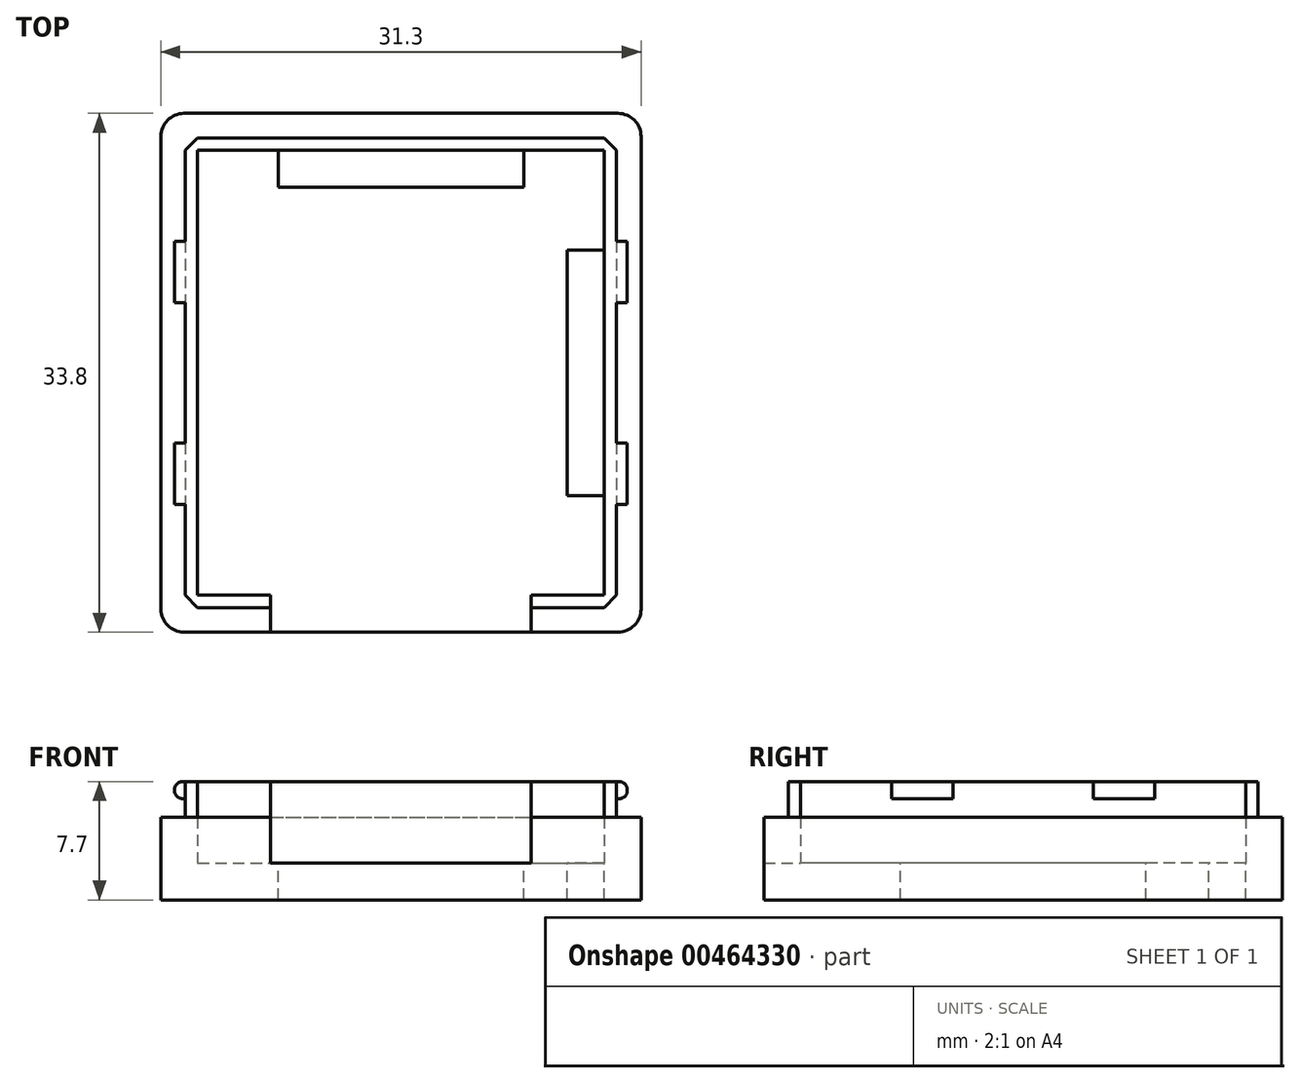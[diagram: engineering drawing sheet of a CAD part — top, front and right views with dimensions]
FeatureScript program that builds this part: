
annotation { "Feature Type Name" : "Feature", "Feature Type Description" : "" }
export const myFeature = defineFeature(function(context is Context, id is Id, definition is map)
    precondition{}
    {
        {
            var Q0;
            Q0=qCreatedBy(makeId("Top.planeOp"),FACE);
            var sketch = newSketch(context, id + "F0", { "sketchPlane" : qUnion([Q0])});
            skLineSegment(sketch, "E0.bottom", {"start": v(-13.25, 14.5) * mm, "end": v(13.25, 14.5) * mm});
            skLineSegment(sketch, "E0.top", {"start": v(-13.25, -14.5) * mm, "end": v(13.25, -14.5) * mm});
            skLineSegment(sketch, "E0.left", {"start": v(-13.25, 14.5) * mm, "end": v(-13.25, -14.5) * mm});
            skLineSegment(sketch, "E0.right", {"start": v(13.25, 14.5) * mm, "end": v(13.25, -14.5) * mm});
            skPoint(sketch, "E0.middle", {"position": v(0, 0) * mm});
            skLineSegment(sketch, "E1.bottom", {"start": v(-15.65, 16.9) * mm, "end": v(15.65, 16.9) * mm});
            skLineSegment(sketch, "E1.top", {"start": v(-15.65, -16.9) * mm, "end": v(15.65, -16.9) * mm});
            skLineSegment(sketch, "E1.left", {"start": v(-15.65, 16.9) * mm, "end": v(-15.65, -16.9) * mm});
            skLineSegment(sketch, "E1.right", {"start": v(15.65, 16.9) * mm, "end": v(15.65, -16.9) * mm});
            skLineSegment(sketch, "E2.bottom", {"start": v(-8, 14.5) * mm, "end": v(8, 14.5) * mm});
            skLineSegment(sketch, "E2.top", {"start": v(-8, 12.1) * mm, "end": v(8, 12.1) * mm});
            skLineSegment(sketch, "E2.left", {"start": v(-8, 14.5) * mm, "end": v(-8, 12.1) * mm});
            skLineSegment(sketch, "E2.right", {"start": v(8, 14.5) * mm, "end": v(8, 12.1) * mm});
            skLineSegment(sketch, "E3.bottom", {"start": v(-13.25, 8) * mm, "end": v(-10.85, 8) * mm});
            skLineSegment(sketch, "E3.top", {"start": v(-13.25, -8) * mm, "end": v(-10.85, -8) * mm});
            skLineSegment(sketch, "E3.left", {"start": v(-13.25, 8) * mm, "end": v(-13.25, -8) * mm});
            skLineSegment(sketch, "E3.right", {"start": v(-10.85, 8) * mm, "end": v(-10.85, -8) * mm});
            skLineSegment(sketch, "E4.MirrorCS", {"start": v(8, -14.5) * mm, "end": v(8, -12.1) * mm});
            skLineSegment(sketch, "E5.MirrorCS", {"start": v(-8, -14.5) * mm, "end": v(-8, -12.1) * mm});
            skLineSegment(sketch, "E6.MirrorCS", {"start": v(-8, -14.5) * mm, "end": v(8, -14.5) * mm});
            skLineSegment(sketch, "E7.MirrorCS", {"start": v(-8, -12.1) * mm, "end": v(8, -12.1) * mm});
            skLineSegment(sketch, "E8.MirrorCS", {"start": v(13.25, 8) * mm, "end": v(13.25, -8) * mm});
            skLineSegment(sketch, "E9.MirrorCS", {"start": v(13.25, -8) * mm, "end": v(10.85, -8) * mm});
            skLineSegment(sketch, "E10.MirrorCS", {"start": v(13.25, 8) * mm, "end": v(10.85, 8) * mm});
            skLineSegment(sketch, "E11.MirrorCS", {"start": v(10.85, 8) * mm, "end": v(10.85, -8) * mm});
            skSolve(sketch);
        }
        {
            var Q0;
            Q0=makeQuery(id+"F0.imprint","IMPRINT",FACE,{"disambiguationData":[TD([[makeQuery(id+"F0.imprint","IMPRINT",EDGE,{"derivedFrom":sQuery(id+"F0.wireOp",EDGE,"E0.bottom")}),-1.0]])]});
            var Q1;
            Q1=makeQuery(id+"F0.imprint","IMPRINT",FACE,{"disambiguationData":[TD([[makeQuery(id+"F0.imprint","IMPRINT",EDGE,{"derivedFrom":sQuery(id+"F0.wireOp",EDGE,"E4.MirrorCS")}),1.0]])]});
            var Q2;
            Q2=makeQuery(id+"F0.imprint","IMPRINT",FACE,{"disambiguationData":[TD([[makeQuery(id+"F0.imprint","IMPRINT",EDGE,{"derivedFrom":sQuery(id+"F0.wireOp",EDGE,"E3.bottom")}),-1.0]])]});
            var Q3;
            Q3=makeQuery(id+"F0.imprint","IMPRINT",FACE,{"disambiguationData":[TD([[makeQuery(id+"F0.imprint","IMPRINT",EDGE,{"derivedFrom":sQuery(id+"F0.wireOp",EDGE,"E8.MirrorCS")}),-1.0]])]});
            var Q4;
            Q4=makeQuery(id+"F0.imprint","IMPRINT",FACE,{"disambiguationData":[TD([[makeQuery(id+"F0.imprint","IMPRINT",EDGE,{"derivedFrom":sQuery(id+"F0.wireOp",EDGE,"E2.bottom")}),-1.0]])]});
            extrude(context, id + "F1", {"entities" : qUnion([Q0, Q1, Q2, Q3, Q4]), "oppositeDirection" : true, "depth" : 3.4 * mm, "hasSecondDirection" : true, "secondDirectionOppositeDirection" : true, "secondDirectionDepth" : 1 * mm, "offsetDistance" : 25 * mm});
        }
        {
            var Q0;
            Q0=makeQuery(id+"F0.imprint","IMPRINT",FACE,{"disambiguationData":[TD([[makeQuery(id+"F0.imprint","IMPRINT",EDGE,{"derivedFrom":sQuery(id+"F0.wireOp",EDGE,"E0.bottom")}),1.0]])]});
            extrude(context, id + "F2", {"entities" : qUnion([Q0]), "operationType" : NewBodyOperationType.ADD, "depth" : 2 * mm, "hasSecondDirection" : true, "secondDirectionOppositeDirection" : true, "secondDirectionDepth" : 3.4 * mm, "offsetDistance" : 25 * mm});
        }
        {
            var Q0;
            Q0=qCreatedBy(makeId("Top.planeOp"),FACE);
            var sketch = newSketch(context, id + "F3", { "sketchPlane" : qUnion([Q0])});
            skLineSegment(sketch, "E12.bottom", {"start": v(-13.25, 8.57) * mm, "end": v(-14.25, 8.57) * mm});
            skLineSegment(sketch, "E12.top", {"start": v(-13.25, 4.57) * mm, "end": v(-14.25, 4.57) * mm});
            skLineSegment(sketch, "E12.left", {"start": v(-13.25, 8.57) * mm, "end": v(-13.25, 4.57) * mm});
            skLineSegment(sketch, "E13.MirrorCS", {"start": v(13.25, 8.57) * mm, "end": v(14.25, 8.57) * mm});
            skLineSegment(sketch, "E14.MirrorCS", {"start": v(13.25, 4.57) * mm, "end": v(14.25, 4.57) * mm});
            skLineSegment(sketch, "E15.MirrorCS", {"start": v(14.25, 8.57) * mm, "end": v(14.25, 4.57) * mm});
            skLineSegment(sketch, "E16.MirrorCS", {"start": v(13.25, 8.57) * mm, "end": v(13.25, 4.57) * mm});
            skLineSegment(sketch, "E17.MirrorCS", {"start": v(14.05, 8.57) * mm, "end": v(14.05, 4.57) * mm});
            skLineSegment(sketch, "E18.bottom", {"start": v(-14.25, 8.57) * mm, "end": v(-14.75, 8.57) * mm});
            skLineSegment(sketch, "E18.top", {"start": v(-14.25, 4.57) * mm, "end": v(-14.75, 4.57) * mm});
            skLineSegment(sketch, "E18.right", {"start": v(-14.75, 8.57) * mm, "end": v(-14.75, 4.57) * mm});
            skLineSegment(sketch, "E19.MirrorCS", {"start": v(14.25, 4.57) * mm, "end": v(14.75, 4.57) * mm});
            skLineSegment(sketch, "E20.MirrorCS", {"start": v(14.75, 8.57) * mm, "end": v(14.75, 4.57) * mm});
            skLineSegment(sketch, "E21.MirrorCS", {"start": v(14.25, 8.57) * mm, "end": v(14.75, 8.57) * mm});
            skLineSegment(sketch, "E22", {"start": v(-14.25, 8.57) * mm, "end": v(-14.25, 4.57) * mm});
            skLineSegment(sketch, "E23", {"start": v(-14.05, 8.57) * mm, "end": v(-14.05, 4.57) * mm});
            skLineSegment(sketch, "E24.MirrorCS", {"start": v(-14.25, -8.57) * mm, "end": v(-14.75, -8.57) * mm});
            skLineSegment(sketch, "E25.MirrorCS", {"start": v(-13.25, -8.57) * mm, "end": v(-14.25, -8.57) * mm});
            skLineSegment(sketch, "E26.MirrorCS", {"start": v(-14.75, -8.57) * mm, "end": v(-14.75, -4.57) * mm});
            skLineSegment(sketch, "E27.MirrorCS", {"start": v(-14.25, -4.57) * mm, "end": v(-14.75, -4.57) * mm});
            skLineSegment(sketch, "E28.MirrorCS", {"start": v(-14.05, -8.57) * mm, "end": v(-14.05, -4.57) * mm});
            skLineSegment(sketch, "E29.MirrorCS", {"start": v(-13.25, -8.57) * mm, "end": v(-13.25, -4.57) * mm});
            skLineSegment(sketch, "E30.MirrorCS", {"start": v(-14.25, -8.57) * mm, "end": v(-14.25, -4.57) * mm});
            skLineSegment(sketch, "E31.MirrorCS", {"start": v(-13.25, -4.57) * mm, "end": v(-14.25, -4.57) * mm});
            skLineSegment(sketch, "E32.MirrorCS", {"start": v(14.25, -4.57) * mm, "end": v(14.75, -4.57) * mm});
            skLineSegment(sketch, "E33.MirrorCS", {"start": v(14.25, -8.57) * mm, "end": v(14.75, -8.57) * mm});
            skLineSegment(sketch, "E34.MirrorCS", {"start": v(14.75, -8.57) * mm, "end": v(14.75, -4.57) * mm});
            skLineSegment(sketch, "E35.MirrorCS", {"start": v(14.05, -8.57) * mm, "end": v(14.05, -4.57) * mm});
            skLineSegment(sketch, "E36.MirrorCS", {"start": v(13.25, -8.57) * mm, "end": v(13.25, -4.57) * mm});
            skLineSegment(sketch, "E37.MirrorCS", {"start": v(13.25, -4.57) * mm, "end": v(14.25, -4.57) * mm});
            skLineSegment(sketch, "E38.MirrorCS", {"start": v(14.25, -8.57) * mm, "end": v(14.25, -4.57) * mm});
            skLineSegment(sketch, "E39.MirrorCS", {"start": v(13.25, -8.57) * mm, "end": v(14.25, -8.57) * mm});
            skSolve(sketch);
        }
        {
            var Q0;
            Q0=makeQuery(id+"F2.opExtrude","CAP_FACE",FACE,{"disambiguationData":[OSD([sQuery(id+"F0.wireOp",EDGE,"E0.bottom"),sQuery(id+"F0.wireOp",EDGE,"E0.top"),sQuery(id+"F0.wireOp",EDGE,"E0.left"),sQuery(id+"F0.wireOp",EDGE,"E0.right"),sQuery(id+"F0.wireOp",EDGE,"E1.bottom"),sQuery(id+"F0.wireOp",EDGE,"E1.top"),sQuery(id+"F0.wireOp",EDGE,"E1.left"),sQuery(id+"F0.wireOp",EDGE,"E1.right"),sQuery(id+"F0.wireOp",EDGE,"E2.bottom"),sQuery(id+"F0.wireOp",EDGE,"E3.left"),sQuery(id+"F0.wireOp",EDGE,"E6.MirrorCS"),sQuery(id+"F0.wireOp",EDGE,"E8.MirrorCS")])],"isStart":false});
            var sketch = newSketch(context, id + "F4", { "sketchPlane" : qUnion([Q0])});
            skLineSegment(sketch, "E40.bottom", {"start": v(-13.25, 14.5) * mm, "end": v(13.25, 14.5) * mm});
            skLineSegment(sketch, "E40.top", {"start": v(-13.25, -14.5) * mm, "end": v(13.25, -14.5) * mm});
            skLineSegment(sketch, "E40.left", {"start": v(-13.25, 14.5) * mm, "end": v(-13.25, -14.5) * mm});
            skLineSegment(sketch, "E40.right", {"start": v(13.25, 14.5) * mm, "end": v(13.25, -14.5) * mm});
            skLineSegment(sketch, "E41.bottom", {"start": v(-14.05, 15.3) * mm, "end": v(14.05, 15.3) * mm});
            skLineSegment(sketch, "E41.top", {"start": v(-14.05, -15.3) * mm, "end": v(14.05, -15.3) * mm});
            skLineSegment(sketch, "E41.left", {"start": v(-14.05, 15.3) * mm, "end": v(-14.05, -15.3) * mm});
            skLineSegment(sketch, "E41.right", {"start": v(14.05, 15.3) * mm, "end": v(14.05, -15.3) * mm});
            skSolve(sketch);
        }
        {
            var Q0;
            Q0 = qSketchRegion(id + "F4", true);
            extrude(context, id + "F5", {"entities" : qUnion([Q0]), "operationType" : NewBodyOperationType.ADD, "depth" : 2.3 * mm, "offsetDistance" : 25 * mm});
        }
        {
            var Q0;
            Q0=qSketchRegion(id+"F3",true);
            extrude(context, id + "F6", {"entities" : qUnion([Q0]), "operationType" : NewBodyOperationType.ADD, "depth" : 2 * mm, "hasSecondDirection" : true, "secondDirectionOppositeDirection" : false, "secondDirectionDepth" : 1.2 * mm});
        }
        {
            var Q0;
            {var subQ2=sQuery(id+"F3.wireOp",EDGE,"E28.MirrorCS");Q0=makeQuery(id+"F3.imprint","IMPRINT",FACE,{"disambiguationData":[TD([[makeQuery(id+"F3.imprint","IMPRINT",EDGE,{"derivedFrom":subQ2}),-1.0]])]});}
            var Q1;
            {var subQ0=sQuery(id+"F3.wireOp",EDGE,"E12.left");Q1=makeQuery(id+"F3.imprint","IMPRINT",FACE,{"disambiguationData":[TD([[makeQuery(id+"F3.imprint","IMPRINT",EDGE,{"derivedFrom":subQ0}),-1.0]])]});}
            var Q2;
            {var subQ0=sQuery(id+"F3.wireOp",EDGE,"E35.MirrorCS");Q2=makeQuery(id+"F3.imprint","IMPRINT",FACE,{"disambiguationData":[TD([[makeQuery(id+"F3.imprint","IMPRINT",EDGE,{"derivedFrom":subQ0}),1.0]])]});}
            var Q3;
            {var subQ0=sQuery(id+"F3.wireOp",EDGE,"E16.MirrorCS");Q3=makeQuery(id+"F3.imprint","IMPRINT",FACE,{"disambiguationData":[TD([[makeQuery(id+"F3.imprint","IMPRINT",EDGE,{"derivedFrom":subQ0}),1.0]])]});}
            extrude(context, id + "F7", {"entities" : qUnion([Q0, Q1, Q2, Q3]), "operationType" : NewBodyOperationType.ADD, "depth" : 4.3 * mm, "hasSecondDirection" : true, "secondDirectionOppositeDirection" : false, "secondDirectionDepth" : 2 * mm});
        }
        {
            var Q0;
            Q0=makeQuery(id+"F3.imprint","IMPRINT",FACE,{"disambiguationData":[TD([[makeQuery(id+"F3.imprint","IMPRINT",EDGE,{"derivedFrom":sQuery(id+"F3.wireOp",EDGE,"E18.bottom")}),1.0]])]});
            var Q1;
            {var subQ0=sQuery(id+"F3.wireOp",EDGE,"E22");Q1=makeQuery(id+"F3.imprint","IMPRINT",FACE,{"disambiguationData":[TD([[makeQuery(id+"F3.imprint","IMPRINT",EDGE,{"derivedFrom":subQ0}),1.0]])]});}
            var Q2;
            Q2=makeQuery(id+"F3.imprint","IMPRINT",FACE,{"disambiguationData":[TD([[makeQuery(id+"F3.imprint","IMPRINT",EDGE,{"derivedFrom":sQuery(id+"F3.wireOp",EDGE,"E24.MirrorCS")}),-1.0]])]});
            var Q3;
            {var subQ2=sQuery(id+"F3.wireOp",EDGE,"E28.MirrorCS");Q3=makeQuery(id+"F3.imprint","IMPRINT",FACE,{"disambiguationData":[TD([[makeQuery(id+"F3.imprint","IMPRINT",EDGE,{"derivedFrom":subQ2}),1.0]])]});}
            var Q4;
            Q4=makeQuery(id+"F3.imprint","IMPRINT",FACE,{"disambiguationData":[TD([[makeQuery(id+"F3.imprint","IMPRINT",EDGE,{"derivedFrom":sQuery(id+"F3.wireOp",EDGE,"E15.MirrorCS")}),1.0]])]});
            var Q5;
            {var subQ0=sQuery(id+"F3.wireOp",EDGE,"E15.MirrorCS");Q5=makeQuery(id+"F3.imprint","IMPRINT",FACE,{"disambiguationData":[TD([[makeQuery(id+"F3.imprint","IMPRINT",EDGE,{"derivedFrom":subQ0}),-1.0]])]});}
            var Q6;
            Q6=makeQuery(id+"F3.imprint","IMPRINT",FACE,{"disambiguationData":[TD([[makeQuery(id+"F3.imprint","IMPRINT",EDGE,{"derivedFrom":sQuery(id+"F3.wireOp",EDGE,"E32.MirrorCS")}),-1.0]])]});
            var Q7;
            {var subQ0=sQuery(id+"F3.wireOp",EDGE,"E35.MirrorCS");Q7=makeQuery(id+"F3.imprint","IMPRINT",FACE,{"disambiguationData":[TD([[makeQuery(id+"F3.imprint","IMPRINT",EDGE,{"derivedFrom":subQ0}),-1.0]])]});}
            extrude(context, id + "F8", {"entities" : qUnion([Q0, Q1, Q2, Q3, Q4, Q5, Q6, Q7]), "operationType" : NewBodyOperationType.ADD, "depth" : 4.3 * mm, "hasSecondDirection" : true, "secondDirectionOppositeDirection" : false, "secondDirectionDepth" : 3.2 * mm});
        }
        {
            var Q0;
            Q0=makeQuery(id+"F6.opExtrude","CAP_EDGE",EDGE,{"disambiguationData":[OSD([sQuery(id+"F3.wireOp",EDGE,"VDrkBrkV-ZUyN-kKdc-6HjS-wqe3Krwlsqec.left")])],"isStart":true});
            var Q1;
            Q1=makeQuery(id+"F6.opExtrude","CAP_EDGE",EDGE,{"disambiguationData":[OSD([sQuery(id+"F3.wireOp",EDGE,"E12.left")])],"isStart":true});
            var Q2;
            Q2=makeQuery(id+"F6.opExtrude","CAP_EDGE",EDGE,{"disambiguationData":[OSD([sQuery(id+"F3.wireOp",EDGE,"9b8740c0-6d80-43f4-a298-cfb8220f7c486.MirrorCS")])],"isStart":true});
            var Q3;
            Q3=makeQuery(id+"F6.opExtrude","CAP_EDGE",EDGE,{"disambiguationData":[OSD([sQuery(id+"F3.wireOp",EDGE,"E16.MirrorCS")])],"isStart":true});
            var Q4;
            Q4=makeQuery(id+"F8.opExtrude","CAP_EDGE",EDGE,{"disambiguationData":[OSD([sQuery(id+"F3.wireOp",EDGE,"13b3b95b-50e3-4c5a-a444-739a302621f31.MirrorCS")])],"isStart":true});
            var Q5;
            Q5=makeQuery(id+"F8.opExtrude","CAP_EDGE",EDGE,{"disambiguationData":[OSD([sQuery(id+"F3.wireOp",EDGE,"13b3b95b-50e3-4c5a-a444-739a302621f31.MirrorCS")])],"isStart":false});
            var Q6;
            Q6=makeQuery(id+"F8.opExtrude","CAP_EDGE",EDGE,{"disambiguationData":[OSD([sQuery(id+"F3.wireOp",EDGE,"E20.MirrorCS")])],"isStart":true});
            var Q7;
            Q7=makeQuery(id+"F8.opExtrude","CAP_EDGE",EDGE,{"disambiguationData":[OSD([sQuery(id+"F3.wireOp",EDGE,"6daNayIJ-oZqj-4Qv5-FHtt-P2iYpOLPTab5.right")])],"isStart":true});
            var Q8;
            Q8=makeQuery(id+"F8.opExtrude","CAP_EDGE",EDGE,{"disambiguationData":[OSD([sQuery(id+"F3.wireOp",EDGE,"E18.right")])],"isStart":true});
            var Q9;
            Q9=makeQuery(id+"F8.opExtrude","CAP_EDGE",EDGE,{"disambiguationData":[OSD([sQuery(id+"F3.wireOp",EDGE,"E18.right")])],"isStart":false});
            var Q10;
            Q10=makeQuery(id+"F8.opExtrude","CAP_EDGE",EDGE,{"disambiguationData":[OSD([sQuery(id+"F3.wireOp",EDGE,"6daNayIJ-oZqj-4Qv5-FHtt-P2iYpOLPTab5.right")])],"isStart":false});
            var Q11;
            Q11=makeQuery(id+"F8.opExtrude","CAP_EDGE",EDGE,{"disambiguationData":[OSD([sQuery(id+"F3.wireOp",EDGE,"E34.MirrorCS")])],"isStart":false});
            var Q12;
            Q12=makeQuery(id+"F8.opExtrude","CAP_EDGE",EDGE,{"disambiguationData":[OSD([sQuery(id+"F3.wireOp",EDGE,"E34.MirrorCS")])],"isStart":true});
            var Q13;
            Q13=makeQuery(id+"F6.opExtrude","CAP_EDGE",EDGE,{"disambiguationData":[OSD([sQuery(id+"F3.wireOp",EDGE,"E36.MirrorCS")])],"isStart":true});
            var Q14;
            Q14=makeQuery(id+"F8.opExtrude","CAP_EDGE",EDGE,{"disambiguationData":[OSD([sQuery(id+"F3.wireOp",EDGE,"E26.MirrorCS")])],"isStart":false});
            var Q15;
            Q15=makeQuery(id+"F8.opExtrude","CAP_EDGE",EDGE,{"disambiguationData":[OSD([sQuery(id+"F3.wireOp",EDGE,"E26.MirrorCS")])],"isStart":true});
            var Q16;
            Q16=makeQuery(id+"F6.opExtrude","CAP_EDGE",EDGE,{"disambiguationData":[OSD([sQuery(id+"F3.wireOp",EDGE,"E29.MirrorCS")])],"isStart":true});
            var Q17;
            Q17=makeQuery(id+"F8.opExtrude","CAP_EDGE",EDGE,{"disambiguationData":[OSD([sQuery(id+"F3.wireOp",EDGE,"E20.MirrorCS")])],"isStart":false});
            fillet(context, id + "F9", {"entities" : qUnion([Q0, Q1, Q2, Q3, Q4, Q5, Q6, Q7, Q8, Q9, Q10, Q11, Q12, Q13, Q14, Q15, Q16, Q17]), "radius" : .5 * mm, "tangentPropagation" : true, "allowEdgeOverflow" : false});
        }
        {
            var Q0;
            Q0=qCreatedBy(makeId("Front.planeOp"),FACE);
            var sketch = newSketch(context, id + "F10", { "sketchPlane" : qUnion([Q0])});
            skLineSegment(sketch, "E42.bottom", {"start": v(-8.5, 6) * mm, "end": v(8.5, 6) * mm});
            skLineSegment(sketch, "E42.top", {"start": v(-8.5, -1) * mm, "end": v(8.5, -1) * mm});
            skLineSegment(sketch, "E42.left", {"start": v(-8.5, 6) * mm, "end": v(-8.5, -1) * mm});
            skLineSegment(sketch, "E42.right", {"start": v(8.5, 6) * mm, "end": v(8.5, -1) * mm});
            skPoint(sketch, "E43", {"position": v(0, 7) * mm});
            skSolve(sketch);
        }
        {
            var Q0;
            Q0=qSketchRegion(id+"F10",true);
            extrude(context, id + "F11", {"entities" : qUnion([Q0]), "operationType" : NewBodyOperationType.REMOVE, "depth" : 18 * mm, "hasSecondDirection" : true, "secondDirectionOppositeDirection" : false, "secondDirectionDepth" : 14 * mm, "offsetDistance" : 25 * mm});
        }
        {
            var Q0;
            Q0=makeQuery(id+"F2.opExtrude","SWEPT_EDGE",EDGE,{"disambiguationData":[OSD([sQuery(id+"F0.wireOp",EDGE,"E1.top"),sQuery(id+"F0.wireOp",EDGE,"E1.right")])]});
            var Q1;
            Q1=makeQuery(id+"F2.opExtrude","SWEPT_EDGE",EDGE,{"disambiguationData":[OSD([sQuery(id+"F0.wireOp",EDGE,"E1.bottom"),sQuery(id+"F0.wireOp",EDGE,"E1.right")])]});
            var Q2;
            Q2=makeQuery(id+"F2.opExtrude","SWEPT_EDGE",EDGE,{"disambiguationData":[OSD([sQuery(id+"F0.wireOp",EDGE,"E1.bottom"),sQuery(id+"F0.wireOp",EDGE,"E1.left")])]});
            var Q3;
            Q3=makeQuery(id+"F2.opExtrude","SWEPT_EDGE",EDGE,{"disambiguationData":[OSD([sQuery(id+"F0.wireOp",EDGE,"E1.top"),sQuery(id+"F0.wireOp",EDGE,"E1.left")])]});
            fillet(context, id + "F12", {"entities" : qUnion([Q0, Q1, Q2, Q3]), "radius" : 1.5 * mm, "tangentPropagation" : true, "allowEdgeOverflow" : false});
        }
        {
            var Q0;
            Q0=qCreatedBy(makeId("Top.planeOp"),FACE);
            var sketch = newSketch(context, id + "F13", { "sketchPlane" : qUnion([Q0])});
            skLineSegment(sketch, "E44.bottom", {"start": v(-17.68, 1.58) * mm, "end": v(-3.99, 1.58) * mm});
            skLineSegment(sketch, "E44.top", {"start": v(-17.68, -19.75) * mm, "end": v(20.4, -19.75) * mm});
            skLineSegment(sketch, "E44.left", {"start": v(-17.68, 1.58) * mm, "end": v(-17.68, -19.75) * mm});
            skLineSegment(sketch, "E44.right", {"start": v(20.4, 1.58) * mm, "end": v(20.4, -19.75) * mm});
            skLineSegment(sketch, "E45.top", {"start": v(-3.99, -11.38) * mm, "end": v(3.99, -11.38) * mm});
            skLineSegment(sketch, "E45.left", {"start": v(-3.99, 1.58) * mm, "end": v(-3.99, -11.38) * mm});
            skLineSegment(sketch, "E45.right", {"start": v(3.99, 1.58) * mm, "end": v(3.99, -11.38) * mm});
            skLineSegment(sketch, "E46.trimOffspring", {"start": v(3.99, 1.58) * mm, "end": v(20.4, 1.58) * mm});
            skSolve(sketch);
        }
        {
            var Q0;
            Q0=makeQuery(id+"F5.opExtrude","SWEPT_EDGE",EDGE,{"disambiguationData":[OSD([sQuery(id+"F4.wireOp",EDGE,"E41.bottom"),sQuery(id+"F4.wireOp",EDGE,"E41.left")])]});
            var Q1;
            Q1=makeQuery(id+"F5.opExtrude","SWEPT_EDGE",EDGE,{"disambiguationData":[OSD([sQuery(id+"F4.wireOp",EDGE,"E41.bottom"),sQuery(id+"F4.wireOp",EDGE,"E41.right")])]});
            var Q2;
            Q2=makeQuery(id+"F5.opExtrude","SWEPT_EDGE",EDGE,{"disambiguationData":[OSD([sQuery(id+"F4.wireOp",EDGE,"E41.top"),sQuery(id+"F4.wireOp",EDGE,"E41.left")])]});
            var Q3;
            Q3=makeQuery(id+"F5.opExtrude","SWEPT_EDGE",EDGE,{"disambiguationData":[OSD([sQuery(id+"F4.wireOp",EDGE,"E41.top"),sQuery(id+"F4.wireOp",EDGE,"E41.right")])]});
            chamfer(context, id + "F14", {"entities" : qUnion([Q0, Q1, Q2, Q3]), "width" : .8 * mm, "tangentPropagation" : true});
        }
    });
